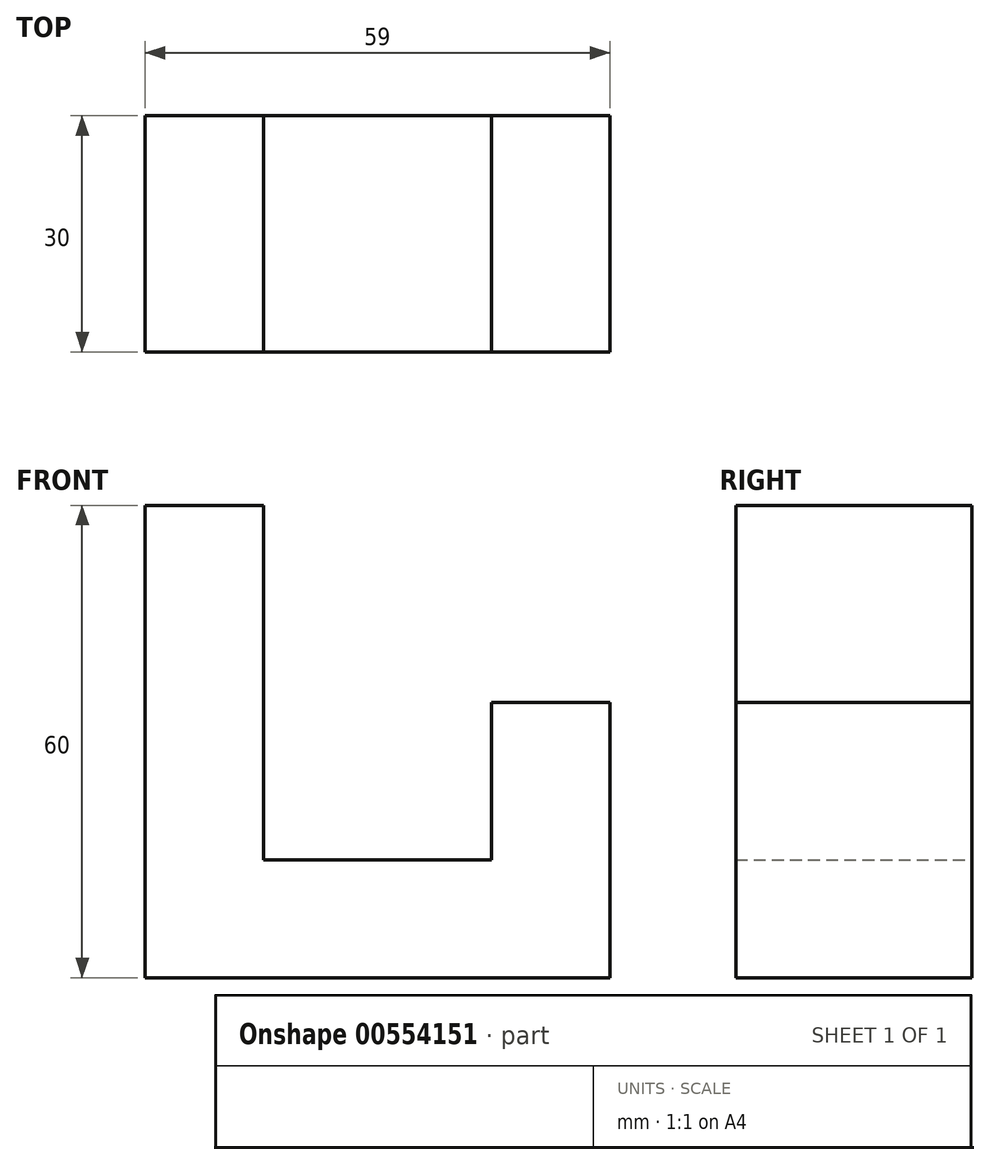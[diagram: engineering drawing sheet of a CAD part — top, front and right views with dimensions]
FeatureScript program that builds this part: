
annotation { "Feature Type Name" : "Feature", "Feature Type Description" : "" }
export const myFeature = defineFeature(function(context is Context, id is Id, definition is map)
    precondition{}
    {
        {
            var Q0;
            Q0=qCreatedBy(makeId("Front.planeOp"),FACE);
            var sketch = newSketch(context, id + "F0", { "sketchPlane" : qUnion([Q0])});
            skLineSegment(sketch, "E0", {"start": v(33.6, 0) * mm, "end": v(33.6, 35) * mm});
            skLineSegment(sketch, "E1", {"start": v(33.6, 35) * mm, "end": v(18.6, 35) * mm});
            skLineSegment(sketch, "E2", {"start": v(18.6, 35) * mm, "end": v(18.6, 15) * mm});
            skLineSegment(sketch, "E3", {"start": v(18.6, 15) * mm, "end": v(-10.4, 15) * mm});
            skLineSegment(sketch, "E4", {"start": v(-10.4, 15) * mm, "end": v(-10.4, 35) * mm});
            skLineSegment(sketch, "E5", {"start": v(-10.4, 35) * mm, "end": v(-25.4, 35) * mm});
            skLineSegment(sketch, "E6", {"start": v(-25.4, 35) * mm, "end": v(-25.4, 0) * mm});
            skLineSegment(sketch, "E7", {"start": v(-25.4, 0) * mm, "end": v(33.6, 0) * mm});
            skSolve(sketch);
        }
        {
            var Q0;
            Q0=makeQuery(id+"F0.imprint","IMPRINT",FACE,{"disambiguationData":[TD([[makeQuery(id+"F0.imprint","IMPRINT",EDGE,{"derivedFrom":sQuery(id+"F0.wireOp",EDGE,"E0")}),1.0]])]});
            extrude(context, id + "F1", {"entities" : qUnion([Q0]), "depth" : 30 * mm, "offsetDistance" : 25 * mm});
        }
        {
            var Q0;
            Q0=makeQuery(id+"F1.opExtrude","SWEPT_FACE",FACE,{"disambiguationData":[OSD([sQuery(id+"F0.wireOp",EDGE,"E5")])]});
            extrude(context, id + "F2", {"entities" : qUnion([Q0]), "operationType" : NewBodyOperationType.ADD, "depth" : 25 * mm, "offsetDistance" : 25 * mm});
        }
    });
